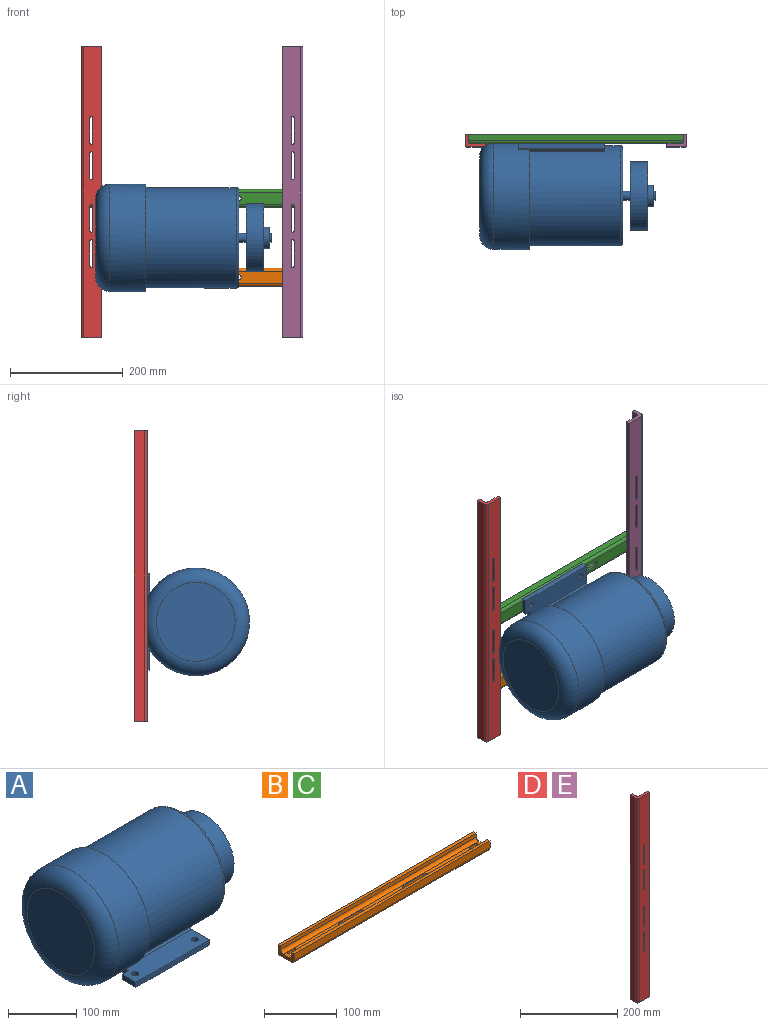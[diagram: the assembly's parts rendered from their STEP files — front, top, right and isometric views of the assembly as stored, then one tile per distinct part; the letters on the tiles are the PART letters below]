
ASSEMBLY  parts=5 mates=11
PART A: 39 faces, bbox 311.2x206.2x206.2 mm
  f0: cylinder r=7.94mm len=15.88mm, axis (-1,0,0), area 633.4mm2, adj f26,f33
  f1: cylinder r=95.25mm len=190.5mm, axis (-1,0,0), area 34747.3mm2, adj f2,f4,f5,f13,f16,f17,f24,f27
  f2: plane 78.38x10.09mm, normal (1,0,0), area 377mm2, adj f1,f3,f4,f16,f29
  f3: cylinder r=88.9mm len=177.8mm, axis (-1,0,0), area 86765.3mm2, adj f2,f4,f5,f10,f16,f17,f21,f27
  f4: plane 139.7x10.09mm, normal (0,-0.71,-0.71), area 1949.2mm2, adj f1,f2,f3,f7,f10,f13
  f5: plane 139.7x5.1mm, normal (0,0.71,0.71), area 965.8mm2, adj f1,f3,f9,f10,f13,f27
  f6: plane 28.58x9.27mm, normal (-1,0,0), area 264.9mm2, adj f7,f8,f9,f14
  f7: plane 152.4x41.28mm, normal (0,0,-1), area 5950.3mm2, adj f4,f6,f8,f10,f11,f12,f13,f14
  f8: plane 152.4x9.27mm, normal (0,1,0), area 1412.9mm2, adj f6,f7,f9,f10
  f9: plane 152.4x37.44mm, normal (0,0,1), area 5413.8mm2, adj f5,f6,f8,f10,f11,f12,f13,f14
  f10: plane 51.36x14.37mm, normal (1,0,0), area 463.5mm2, adj f3,f4,f5,f7,f8,f9
  f11: cylinder r=5.33mm len=10.67mm, axis (0,0,-1), area 310.7mm2, adj f7,f9
  f12: cylinder r=5.33mm len=10.67mm, axis (0,0,-1), area 310.7mm2, adj f7,f9
  f13: plane 17.96x9.71mm, normal (-1,0,0), area 136.5mm2, adj f1,f4,f5,f7,f9,f14
  f14: plane 12.7x9.27mm, normal (0,-1,0), area 117.7mm2, adj f6,f7,f9,f13
  f15: plane 152.4x41.28mm, normal (0,0,-1), area 5950.3mm2, adj f16,f19,f20,f21,f22,f23,f24,f25
  f16: plane 139.7x10.09mm, normal (0,0.71,-0.71), area 1949.2mm2, adj f1,f2,f3,f15,f21,f24
  f17: plane 139.7x5.1mm, normal (0,-0.71,0.71), area 965.8mm2, adj f1,f3,f18,f21,f24,f27
  f18: plane 152.4x37.44mm, normal (0,0,1), area 5413.8mm2, adj f17,f19,f20,f21,f22,f23,f24,f25
  f19: plane 152.4x9.27mm, normal (0,-1,0), area 1412.9mm2, adj f15,f18,f20,f21
  f20: plane 28.58x9.27mm, normal (-1,0,0), area 264.9mm2, adj f15,f18,f19,f25
  f21: plane 51.36x14.37mm, normal (1,0,0), area 463.5mm2, adj f3,f15,f16,f17,f18,f19
  f22: cylinder r=5.33mm len=10.67mm, axis (0,0,-1), area 310.7mm2, adj f15,f18
  f23: cylinder r=5.33mm len=10.67mm, axis (0,0,-1), area 310.7mm2, adj f15,f18
  f24: plane 17.96x9.71mm, normal (-1,0,0), area 136.5mm2, adj f1,f15,f16,f17,f18,f25
  f25: plane 12.7x9.27mm, normal (0,1,0), area 117.7mm2, adj f15,f18,f20,f24
  f26: plane 167.64x167.64mm, normal (1,0,0), area 21874.2mm2, adj f0,f30
  f27: plane 190.5x177.61mm, normal (1,0,0), area 3068.9mm2, adj f1,f3,f5,f17
  f28: plane 139.7x139.7mm, normal (-1,0,0), area 15327.9mm2, adj f31
  f29: plane 75.8x48.78mm, normal (0,0,-1), area 3571.2mm2, adj f1,f2,f31
  f30: torus R=83.82mm, axis (1,0,0), area 4364.7mm2, adj f3,f26
  f31: torus R=69.85mm, axis (1,0,0), area 21070.7mm2, adj f1,f28,f29
  f32: cylinder r=60.32mm len=120.65mm, axis (1,0,0), area 12034.3mm2, adj f33,f34
  f33: plane 120.65x120.65mm, normal (-1,0,0), area 11234.7mm2, adj f0,f32
  f34: plane 120.65x120.65mm, normal (1,0,0), area 10292.5mm2, adj f32,f35
  f35: cylinder r=19.05mm len=38.1mm, axis (-1,0,0), area 1140.1mm2, adj f34,f36
  f36: plane 38.1x38.1mm, normal (1,0,0), area 942.2mm2, adj f35,f38
  f37: plane 15.88x15.88mm, normal (1,0,0), area 197.9mm2, adj f38
  f38: cylinder r=7.94mm len=15.88mm, axis (-1,0,0), area 158.3mm2, adj f36,f37
PART B: 30 faces, bbox 381x31.8x16.5 mm
  f0: plane 381x21.59mm, normal (0,0,-1), area 6989.7mm2, adj f8,f9,f10,f11,f12,f13,f14,f15
  f1: plane 381x11.43mm, normal (0,0,1), area 3118.8mm2, adj f8,f9,f10,f11,f12,f13,f14,f15
  f2: plane 381x5.08mm, normal (0,0,1), area 1935.5mm2, adj f3,f7,f8,f9
  f3: plane 381x11.43mm, normal (0,-1,0), area 4354.8mm2, adj f2,f8,f9,f26
  f4: plane 381x11.43mm, normal (0,1,0), area 4354.8mm2, adj f5,f8,f9,f27
  f5: plane 381x5.08mm, normal (0,0,1), area 1935.5mm2, adj f4,f6,f8,f9
  f6: plane 381x6.35mm, normal (0,-1,0), area 2419.3mm2, adj f5,f8,f9,f28
  f7: plane 381x6.35mm, normal (0,1,0), area 2419.3mm2, adj f2,f8,f9,f29
  f8: plane 31.75x16.51mm, normal (1,0,0), area 277.4mm2, adj f0,f1,f2,f3,f4,f5,f6,f7
  f9: plane 31.75x16.51mm, normal (-1,0,0), area 277.4mm2, adj f0,f1,f2,f3,f4,f5,f6,f7
  f10: plane 14.99x5.08mm, normal (0,1,0), area 76.1mm2, adj f0,f1,f11,f13
  f11: plane 9.91x5.08mm, normal (1,0,0), area 50.3mm2, adj f0,f1,f10,f12
  f12: plane 14.99x5.08mm, normal (0,-1,0), area 76.1mm2, adj f0,f1,f11,f13
  f13: plane 9.91x5.08mm, normal (-1,0,0), area 50.3mm2, adj f0,f1,f10,f12
  f14: plane 39.62x5.08mm, normal (0,-1,0), area 201.3mm2, adj f0,f1,f15,f17
  f15: cylinder r=4.95mm len=9.91mm, axis (0,0,-1), area 79mm2, adj f0,f1,f14,f16
  f16: plane 39.62x5.08mm, normal (0,1,0), area 201.3mm2, adj f0,f1,f15,f17
  f17: cylinder r=4.95mm len=9.91mm, axis (0,0,-1), area 79mm2, adj f0,f1,f14,f16
  f18: cylinder r=4.95mm len=9.91mm, axis (0,0,-1), area 79mm2, adj f0,f1,f19,f21
  f19: plane 39.62x5.08mm, normal (0,-1,0), area 201.3mm2, adj f0,f1,f18,f20
  f20: cylinder r=4.95mm len=9.91mm, axis (0,0,-1), area 79mm2, adj f0,f1,f19,f21
  f21: plane 39.62x5.08mm, normal (0,1,0), area 201.3mm2, adj f0,f1,f18,f20
  f22: plane 14.99x5.08mm, normal (0,1,0), area 76.1mm2, adj f0,f1,f23,f25
  f23: plane 9.91x5.08mm, normal (1,0,0), area 50.3mm2, adj f0,f1,f22,f24
  f24: plane 14.99x5.08mm, normal (0,-1,0), area 76.1mm2, adj f0,f1,f23,f25
  f25: plane 9.91x5.08mm, normal (-1,0,0), area 50.3mm2, adj f0,f1,f22,f24
  f26: cylinder r=5.08mm len=381mm, axis (-1,0,0), area 3040.2mm2, adj f0,f3,f8,f9
  f27: cylinder r=5.08mm len=381mm, axis (-1,0,0), area 3040.2mm2, adj f0,f4,f8,f9
  f28: cylinder r=5.08mm len=381mm, axis (1,0,0), area 3040.2mm2, adj f1,f6,f8,f9
  f29: cylinder r=5.08mm len=381mm, axis (1,0,0), area 3040.2mm2, adj f1,f7,f8,f9
PART C: same geometry as B
PART D: 26 faces, bbox 35.6x22x514.4 mm
  f0: plane 514.35x30.48mm, normal (0,-1,0), area 14856.3mm2, adj f4,f6,f7,f8,f9,f10,f11,f12
  f1: plane 514.35x24.51mm, normal (0,1,0), area 11786.2mm2, adj f4,f6,f7,f8,f9,f10,f11,f12
  f2: plane 514.35x5.97mm, normal (0,1,0), area 3070.2mm2, adj f3,f5,f6,f7
  f3: plane 514.35x16.89mm, normal (-1,0,0), area 8687.9mm2, adj f2,f6,f7,f24
  f4: plane 514.35x5.97mm, normal (1,0,0), area 3070.2mm2, adj f0,f1,f6,f7
  f5: plane 514.35x10.92mm, normal (1,0,0), area 5617.7mm2, adj f2,f6,f7,f25
  f6: plane 35.56x21.97mm, normal (0,0,1), area 307.8mm2, adj f0,f1,f2,f3,f4,f5,f24,f25
  f7: plane 35.56x21.97mm, normal (0,0,-1), area 307.8mm2, adj f0,f1,f2,f3,f4,f5,f24,f25
  f8: plane 45.14x5.97mm, normal (-1,0,0), area 269.5mm2, adj f0,f1,f9,f11
  f9: cylinder r=2.11mm len=5.97mm, axis (0,-1,0), area 39.6mm2, adj f0,f1,f8,f10
  f10: plane 45.99x5.97mm, normal (1,0,0), area 274.5mm2, adj f0,f1,f9,f11
  f11: cylinder r=2.11mm len=5.97mm, axis (0,-1,0), area 39.6mm2, adj f0,f1,f8,f10
  f12: cylinder r=2.11mm len=5.97mm, axis (0,-1,0), area 39.6mm2, adj f0,f1,f13,f15
  f13: plane 45.99x5.97mm, normal (1,0,0), area 274.5mm2, adj f0,f1,f12,f14
  f14: cylinder r=2.11mm len=5.97mm, axis (0,-1,0), area 39.6mm2, adj f0,f1,f13,f15
  f15: plane 45.14x5.97mm, normal (-1,0,0), area 269.5mm2, adj f0,f1,f12,f14
  f16: cylinder r=2.11mm len=5.97mm, axis (0,-1,0), area 39.6mm2, adj f0,f1,f17,f19
  f17: plane 45.99x5.97mm, normal (1,0,0), area 274.5mm2, adj f0,f1,f16,f18
  f18: cylinder r=2.11mm len=5.97mm, axis (0,-1,0), area 39.6mm2, adj f0,f1,f17,f19
  f19: plane 45.14x5.97mm, normal (-1,0,0), area 269.5mm2, adj f0,f1,f16,f18
  f20: cylinder r=2.11mm len=5.97mm, axis (0,-1,0), area 39.6mm2, adj f0,f1,f21,f23
  f21: plane 45.99x5.97mm, normal (1,0,0), area 274.5mm2, adj f0,f1,f20,f22
  f22: cylinder r=2.11mm len=5.97mm, axis (0,-1,0), area 39.6mm2, adj f0,f1,f21,f23
  f23: plane 45.14x5.97mm, normal (-1,0,0), area 269.5mm2, adj f0,f1,f20,f22
  f24: cylinder r=5.08mm len=514.35mm, axis (0,0,-1), area 4104.3mm2, adj f0,f3,f6,f7
  f25: cylinder r=5.08mm len=514.35mm, axis (0,0,1), area 4104.3mm2, adj f1,f5,f6,f7
PART E: same geometry as D
PLACE A rot(axis=(1,0,0),90deg) t=(247.79,5.97,175.97)mm
PLACE B rot(axis=(0,-0.71,-0.71),180deg) t=(386.97,5.97,106.12)mm
PLACE C rot(axis=(0,-0.71,-0.71),180deg) t=(386.97,5.97,245.82)mm
PLACE D at identity fixed
PLACE E rot(axis=(0,1,0),180deg) t=(392.94,0,514.35)mm
MATE planar D.f5 <-> C.f8  axis (1,0,0) through (5.97,16.51,257.18)mm
MATE planar D.f1 <-> B.f0  axis (0,1,0) through (19.88,5.97,281.09)mm
MATE pin_slot A.f11 <-> C.f0  axis (0,1,0) through (233.5,5.97,245.82)mm
MATE planar D.f5 <-> B.f8  axis (1,0,0) through (5.97,16.51,257.18)mm
MATE pin_slot B.f0 <-> A.f22  axis (0,-1,0) through (196.47,5.97,106.12)mm
MATE planar E.f5 <-> C.f9  axis (-1,0,0) through (386.97,16.51,257.18)mm
MATE pin_slot C.f0 <-> A.f12  axis (0,-1,0) through (196.47,5.97,245.82)mm
MATE planar C.f0 <-> E.f1  axis (0,-1,0) through (196.47,5.97,245.82)mm
MATE planar D.f24 <-> E.f24  axis (0,0,-1) through (5.08,5.08,0)mm
MATE planar C.f0 <-> A.f15  axis (0,-1,0) through (196.47,5.97,245.82)mm
MATE planar D.f1 <-> C.f0  axis (0,1,0) through (23.69,5.97,257.18)mm
